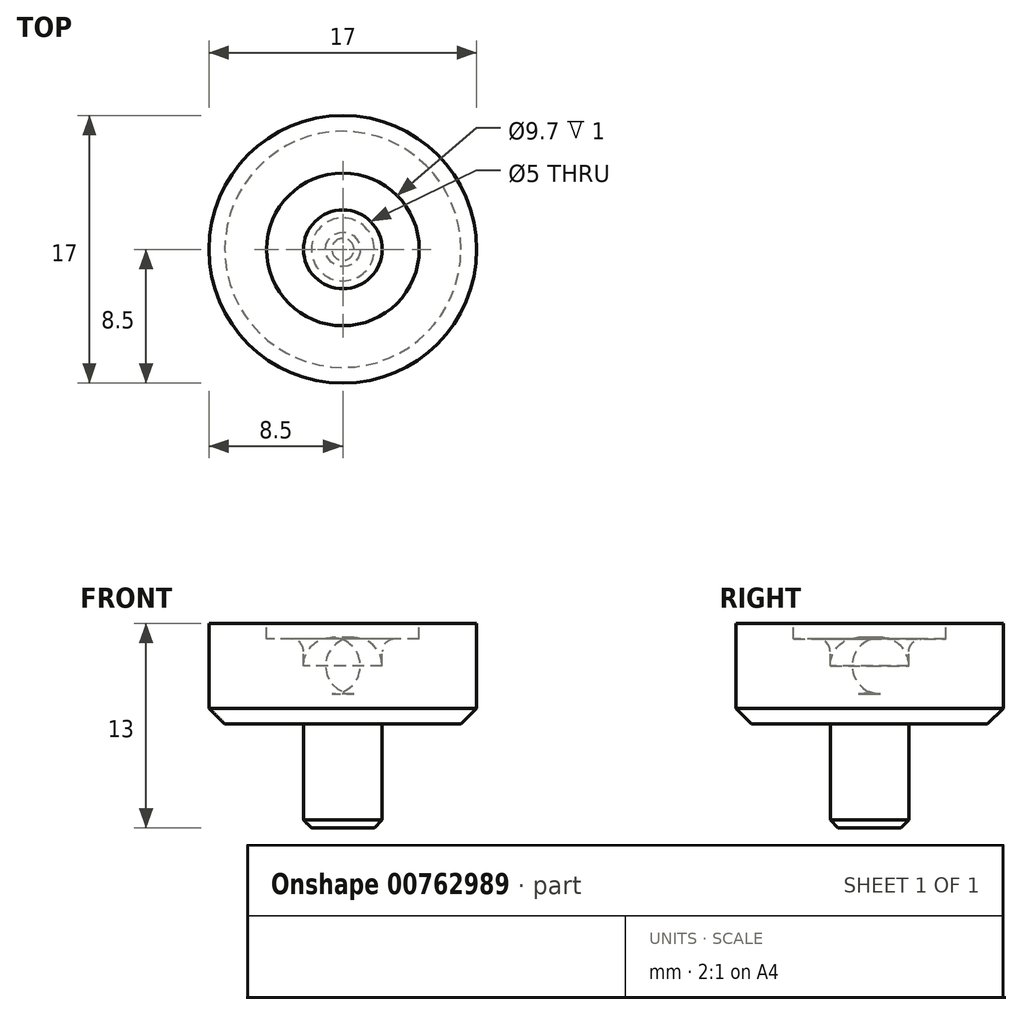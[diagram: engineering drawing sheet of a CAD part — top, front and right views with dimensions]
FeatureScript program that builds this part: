
annotation { "Feature Type Name" : "Feature", "Feature Type Description" : "" }
export const myFeature = defineFeature(function(context is Context, id is Id, definition is map)
    precondition{}
    {
        {
            var Q0;
            Q0=qCreatedBy(makeId("Front.planeOp"),FACE);
            var sketch = newSketch(context, id + "F0", { "sketchPlane" : qUnion([Q0])});
            skLineSegment(sketch, "E0", {"start": v(3.3, 5.4) * mm, "end": v(4.85, 5.4) * mm});
            skLineSegment(sketch, "E1", {"start": v(4.85, 5.4) * mm, "end": v(4.85, 6.4) * mm});
            skLineSegment(sketch, "E2", {"start": v(4.85, 6.4) * mm, "end": v(8.5, 6.4) * mm});
            skLineSegment(sketch, "E3", {"start": v(8.5, 6.4) * mm, "end": v(8.5, 0) * mm});
            skLineSegment(sketch, "E4", {"start": v(8.5, 0) * mm, "end": v(2.5, 0) * mm});
            skLineSegment(sketch, "E5", {"start": v(2.5, 0) * mm, "end": v(2.5, -6.6) * mm});
            skLineSegment(sketch, "E6", {"start": v(2.5, -6.6) * mm, "end": v(0, -6.6) * mm});
            skLineSegment(sketch, "E7", {"start": v(0, 1.9) * mm, "end": v(0, -6.6) * mm});
            skLineSegment(sketch, "E8", {"start": v(2.5, 4.6) * mm, "end": v(2.5, 3.7) * mm});
            skLineSegment(sketch, "E9", {"start": v(0.7, 1.9) * mm, "end": v(0, 1.9) * mm});
            skPoint(sketch, "E10.orphan", {"position": v(0, 5.4) * mm});
            skPoint(sketch, "E11.visualSharp", {"position": v(2.5, 1.9) * mm});
            skArc(sketch, "E11.filletArc", {"start": v(0.7, 1.9) * mm, "mid": v(1.97, 2.43) * mm, "end": v(2.5, 3.7) * mm});
            skPoint(sketch, "E12.visualSharp", {"position": v(2.5, 5.4) * mm});
            skArc(sketch, "E12.filletArc", {"start": v(3.3, 5.4) * mm, "mid": v(2.73, 5.17) * mm, "end": v(2.5, 4.6) * mm});
            skSolve(sketch);
        }
        {
            var Q0;
            Q0=makeQuery(id+"F0.imprint","IMPRINT",FACE,{"disambiguationData":[TD([[makeQuery(id+"F0.imprint","IMPRINT",EDGE,{"derivedFrom":sQuery(id+"F0.wireOp",EDGE,"E0")}),-1.0]])]});
            var Q1;
            Q1=sQuery(id+"F0.wireOp",EDGE,"E7");
            revolve(context, id + "F1", {"surfaceOperationType" : NewSurfaceOperationType.NEW, "entities" : qUnion([Q0]), "axis" : qUnion([Q1]), "revolveType" : RevolveType.FULL});
        }
        {
            var Q0;
            Q0=makeQuery(id+"F1.opRevolve","SWEPT_EDGE",EDGE,{"disambiguationData":[OSD([sQuery(id+"F0.wireOp",EDGE,"E3"),sQuery(id+"F0.wireOp",EDGE,"E4")])]});
            chamfer(context, id + "F2", {"entities" : qUnion([Q0]), "width" : 1 * mm, "tangentPropagation" : true});
        }
        {
            var Q0;
            Q0=makeQuery(id+"F1.opRevolve","SWEPT_EDGE",EDGE,{"disambiguationData":[OSD([sQuery(id+"F0.wireOp",EDGE,"E5"),sQuery(id+"F0.wireOp",EDGE,"E6")])]});
            chamfer(context, id + "F3", {"entities" : qUnion([Q0]), "width" : 0.5 * mm, "tangentPropagation" : true});
        }
    });
